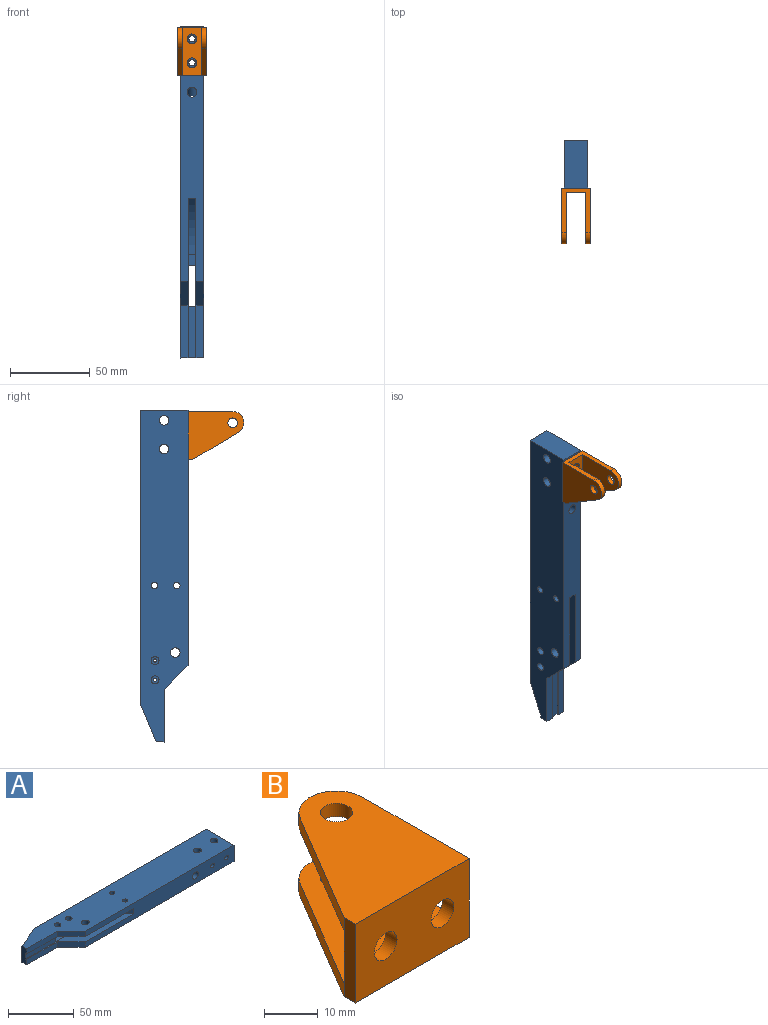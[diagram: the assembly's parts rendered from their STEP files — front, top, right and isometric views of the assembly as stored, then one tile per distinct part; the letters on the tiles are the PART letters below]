
ASSEMBLY  parts=2 mates=1
PART A: 41 faces, bbox 208x31.3x15 mm
  f0: plane 33x5mm, normal (0,-1,0), area 165mm2, adj f1,f3,f7,f32
  f1: plane 15x15mm, normal (-0.71,-0.71,0), area 106.1mm2, adj f0,f2,f7,f32
  f2: plane 160x15mm, normal (0,-1,0), area 2086.6mm2, adj f1,f6,f7,f9,f10,f17,f18,f31
  f3: plane 15x5mm, normal (-1,0,0), area 70mm2, adj f0,f6,f7,f8,f12,f30,f32,f33
  f4: plane 26x0.5mm, normal (0,1,0), area 13mm2, adj f5,f19,f20,f32
  f5: plane 9x6mm, normal (-1,0,0), area 54mm2, adj f4,f20,f21,f22,f28,f29
  f6: plane 208x30mm, normal (0,0,1), area 5363.3mm2, adj f2,f3,f8,f9,f10,f11,f12,f13
  f7: plane 208x30mm, normal (0,0,-1), area 5395.9mm2, adj f0,f1,f2,f3,f10,f11,f12,f13
  f8: plane 33x5mm, normal (0,-1,0), area 165mm2, adj f3,f6,f9,f33
  f9: plane 15x15mm, normal (-0.71,-0.71,0), area 106.1mm2, adj f2,f6,f8,f33
  f10: plane 30x15mm, normal (1,0,0), area 450mm2, adj f2,f6,f7,f11
  f11: plane 184x15mm, normal (0,1,0), area 1793.9mm2, adj f6,f7,f10,f12,f17,f18,f19,f20
  f12: plane 24x15mm, normal (-0.38,0.92,0), area 390mm2, adj f3,f6,f7,f11
  f13: cylinder r=2mm len=15mm, axis (0,0,-1), area 188.5mm2, adj f6,f7
  f14: cylinder r=2mm len=15mm, axis (0,0,-1), area 188.5mm2, adj f6,f7
  f15: cylinder r=3mm len=15mm, axis (0,0,-1), area 248.8mm2, adj f6,f7,f18
  f16: cylinder r=3mm len=15mm, axis (0,0,-1), area 248.7mm2, adj f6,f7,f17
  f17: cylinder r=2mm len=30mm, axis (0,-1,0), area 328.2mm2, adj f2,f11,f16
  f18: cylinder r=2mm len=30mm, axis (0,-1,0), area 328.2mm2, adj f2,f11,f15
  f19: plane 14x6mm, normal (1,0,0), area 84mm2, adj f4,f11,f20,f21,f22,f30
  f20: plane 26x14mm, normal (0,0,1), area 352.4mm2, adj f4,f5,f11,f19,f23,f28,f39,f40
  f21: plane 26x14mm, normal (0,0,-1), area 319.7mm2, adj f5,f11,f19,f22,f24,f28,f37,f38
  f22: plane 26x0.5mm, normal (0,1,0), area 13mm2, adj f5,f19,f21,f33
  f23: plane 5x0.5mm, normal (1,0,0), area 2.5mm2, adj f11,f20,f25,f28
  f24: plane 5x0.5mm, normal (1,0,0), area 2.5mm2, adj f11,f21,f27,f28
  f25: plane 113x5mm, normal (0,0,1), area 565mm2, adj f11,f23,f26,f28
  f26: plane 7x5mm, normal (-1,0,0), area 35mm2, adj f11,f25,f27,f28
  f27: plane 113x5mm, normal (0,0,-1), area 565mm2, adj f11,f24,f26,f28
  f28: plane 113x7mm, normal (0,1,0), area 756.1mm2, adj f5,f20,f21,f23,f24,f25,f26,f27
  f29: plane 7x5mm, normal (0,-1,0), area 35mm2, adj f5,f31,f32,f33
  f30: plane 32x5mm, normal (0,-1,0), area 160mm2, adj f3,f19,f32,f33
  f31: cylinder r=46mm len=34.87mm, axis (0,0,1), area 197.9mm2, adj f2,f29,f32,f33
  f32: plane 99.87x16mm, normal (0,0,1), area 791.4mm2, adj f0,f1,f2,f3,f4,f29,f30,f31
  f33: plane 99.87x16mm, normal (0,0,-1), area 791.4mm2, adj f2,f3,f8,f9,f22,f29,f30,f31
  f34: cylinder r=3mm len=6mm, axis (0,0,1), area 94.2mm2, adj f6,f33
  f35: cylinder r=3mm len=6mm, axis (0,0,1), area 94.2mm2, adj f7,f32
  f36: cylinder r=3mm len=27.5mm, axis (-0.21,0.98,0), area 481.8mm2, adj f2,f28
  f37: cylinder r=2.5mm len=5mm, axis (0,0,1), area 70.7mm2, adj f6,f21
  f38: cylinder r=2.5mm len=5mm, axis (0,0,1), area 70.7mm2, adj f6,f21
  f39: cylinder r=1.03mm len=4.5mm, axis (0,0,-1), area 29mm2, adj f7,f20
  f40: cylinder r=1.03mm len=4.5mm, axis (0,0,-1), area 29mm2, adj f7,f20
PART B: 16 faces, bbox 30x35x18 mm
  f0: plane 28x18mm, normal (1,0,0), area 204mm2, adj f1,f4,f5,f6,f9,f11,f12,f13
  f1: cylinder r=7mm len=13.02mm, axis (0,0,-1), area 54.7mm2, adj f0,f2,f5,f12
  f2: plane 28.58x16.98mm, normal (-0.86,0.51,0), area 99.7mm2, adj f1,f5,f8,f12
  f3: cylinder r=3mm len=6mm, axis (0,0,-1), area 56.5mm2, adj f5,f12
  f4: plane 35x30mm, normal (0,0,1), area 704.4mm2, adj f0,f6,f7,f8,f9,f10
  f5: plane 35x30mm, normal (0,0,-1), area 704.4mm2, adj f0,f1,f2,f3,f8,f9
  f6: cylinder r=7mm len=13.02mm, axis (0,0,-1), area 54.7mm2, adj f0,f4,f7,f13
  f7: plane 28.58x16.98mm, normal (-0.86,0.51,0), area 99.7mm2, adj f4,f6,f8,f13
  f8: plane 18x3mm, normal (-1,0,0), area 54mm2, adj f2,f4,f5,f7,f9,f11
  f9: plane 30x18mm, normal (0,-1,0), area 483.5mm2, adj f0,f4,f5,f8,f14,f15
  f10: cylinder r=3mm len=6mm, axis (0,0,-1), area 56.5mm2, adj f4,f13
  f11: plane 30x12mm, normal (0,1,0), area 303.5mm2, adj f0,f8,f12,f13,f14,f15
  f12: plane 32x30mm, normal (0,0,1), area 614.4mm2, adj f0,f1,f2,f3,f11
  f13: plane 32x30mm, normal (0,0,-1), area 614.4mm2, adj f0,f6,f7,f10,f11
  f14: cylinder r=3mm len=6mm, axis (0,-1,0), area 56.5mm2, adj f9,f11
  f15: cylinder r=3mm len=6mm, axis (0,-1,0), area 56.5mm2, adj f9,f11
PLACE A rot(axis=(0,-1,0),90deg) t=(58.29,-36.05,127.15)mm
PLACE B rot(axis=(-0.71,0,-0.71),180deg) t=(58.29,-66.05,126.15)mm
MATE revolute B.f15 <-> A.f18  axis (0,1,0) through (58.29,-66.05,104.15)mm
